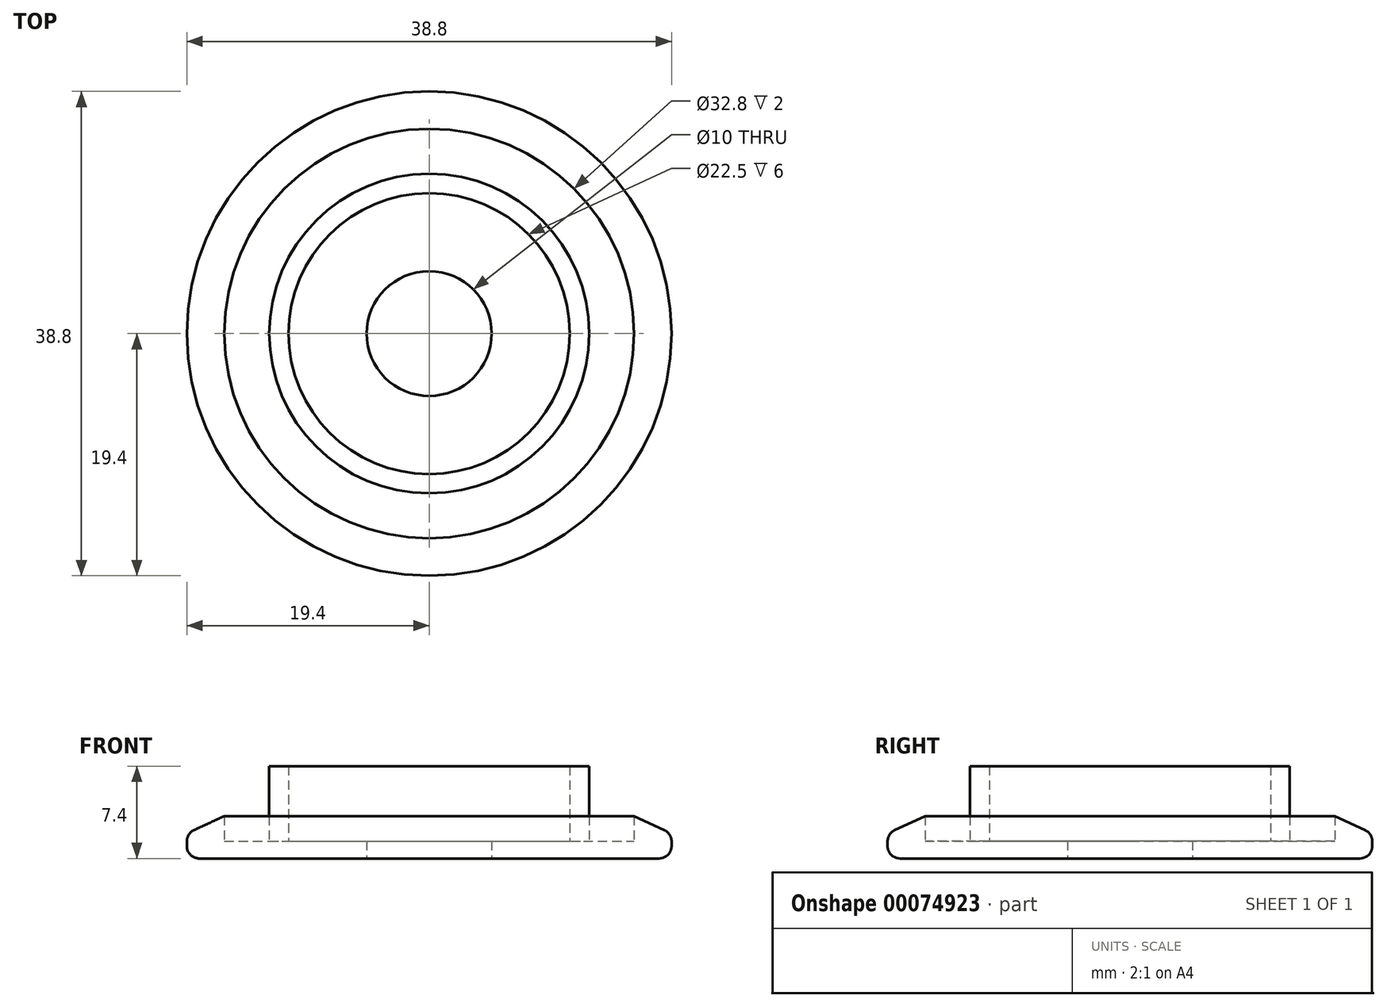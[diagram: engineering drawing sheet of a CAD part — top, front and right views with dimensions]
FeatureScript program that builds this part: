
annotation { "Feature Type Name" : "Feature", "Feature Type Description" : "" }
export const myFeature = defineFeature(function(context is Context, id is Id, definition is map)
    precondition{}
    {
        {
            var Q0;
            Q0=qCreatedBy(makeId("Front.planeOp"),FACE);
            var sketch = newSketch(context, id + "F0", { "sketchPlane" : qUnion([Q0])});
            skLineSegment(sketch, "E0", {"start": v(-5, 0) * mm, "end": v(-19.4, 0) * mm});
            skLineSegment(sketch, "E1", {"start": v(-19.4, 2) * mm, "end": v(-16.4, 3.4) * mm});
            skLineSegment(sketch, "E2", {"start": v(-16.4, 3.4) * mm, "end": v(-16.4, 1.4) * mm});
            skLineSegment(sketch, "E3", {"start": v(-16.4, 1.4) * mm, "end": v(-12.8, 1.4) * mm});
            skLineSegment(sketch, "E4", {"start": v(-12.8, 1.4) * mm, "end": v(-12.8, 7.4) * mm});
            skLineSegment(sketch, "E5", {"start": v(-12.8, 7.4) * mm, "end": v(-11.25, 7.4) * mm});
            skLineSegment(sketch, "E6", {"start": v(-11.25, 7.4) * mm, "end": v(-11.25, 1.4) * mm});
            skLineSegment(sketch, "E7", {"start": v(-11.25, 1.4) * mm, "end": v(-5, 1.4) * mm});
            skLineSegment(sketch, "E8", {"start": v(-5, 1.4) * mm, "end": v(-5, 0) * mm});
            skLineSegment(sketch, "E9", {"start": v(0, 0) * mm, "end": v(0, 8.78) * mm, "construction": true});
            skLineSegment(sketch, "E10", {"start": v(-19.4, 2) * mm, "end": v(-19.4, 0) * mm});
            skSolve(sketch);
        }
        {
            var Q0;
            Q0 = qSketchRegion(id + "F0", true);
            var Q1;
            Q1=sQuery(id+"F0.wireOp",EDGE,"E9");
            revolve(context, id + "F1", {"entities" : qUnion([Q0]), "axis" : qUnion([Q1]), "revolveType" : RevolveType.FULL});
        }
        {
            var Q0;
            Q0=makeQuery(id+"F1.opRevolve","SWEPT_EDGE",EDGE,{"disambiguationData":[OSD([sQuery(id+"F0.wireOp",EDGE,"E1"),sQuery(id+"F0.wireOp",EDGE,"E10")])]});
            var Q1;
            Q1=makeQuery(id+"F1.opRevolve","SWEPT_EDGE",EDGE,{"disambiguationData":[OSD([sQuery(id+"F0.wireOp",EDGE,"E0"),sQuery(id+"F0.wireOp",EDGE,"E10")])]});
            fillet(context, id + "F2", {"entities" : qUnion([Q0, Q1]), "radius" : 1 * mm, "tangentPropagation" : true, "allowEdgeOverflow" : false});
        }
    });
